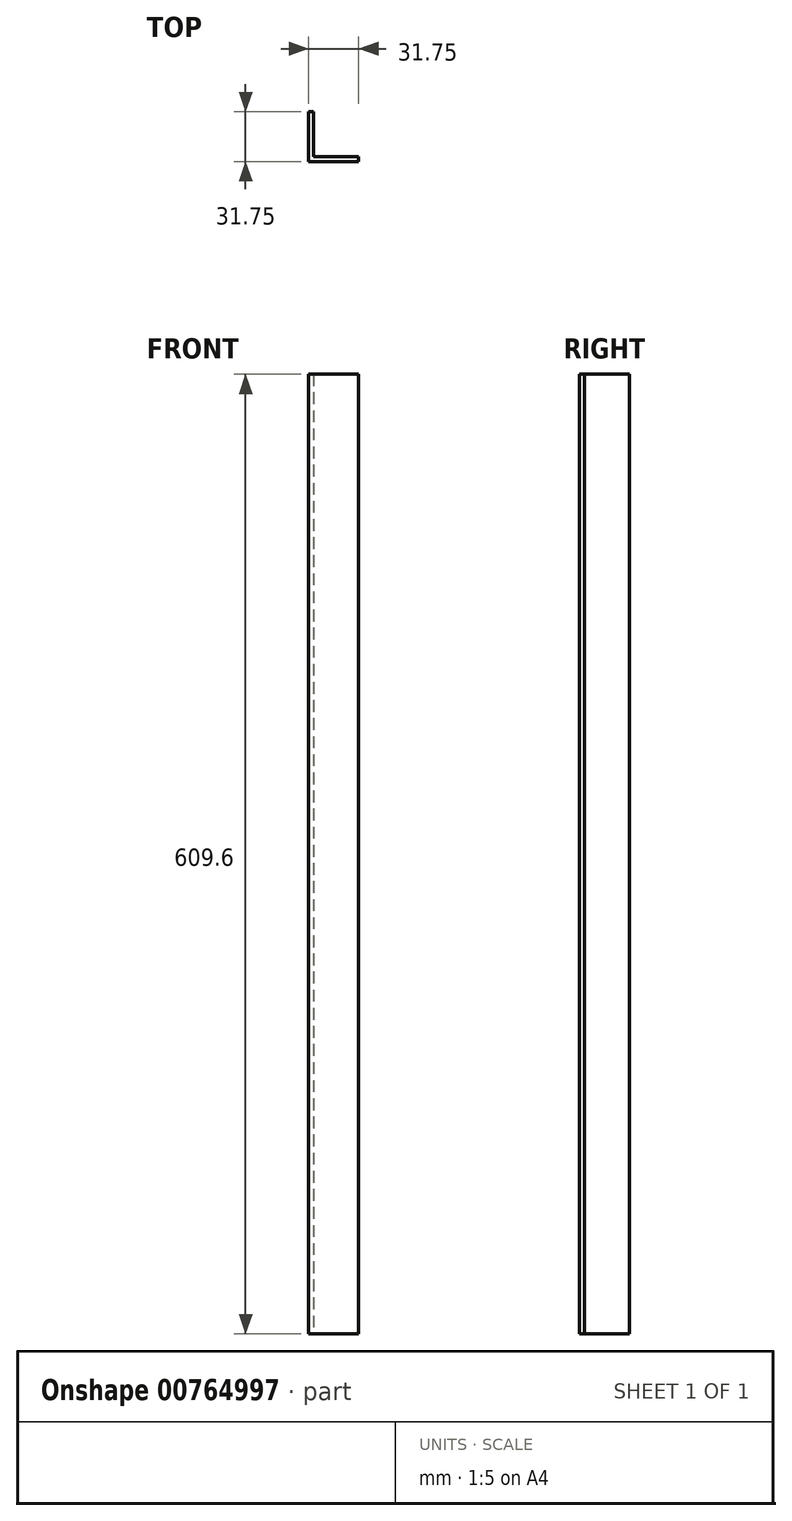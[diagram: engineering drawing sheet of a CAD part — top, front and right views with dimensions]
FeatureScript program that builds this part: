
annotation { "Feature Type Name" : "Feature", "Feature Type Description" : "" }
export const myFeature = defineFeature(function(context is Context, id is Id, definition is map)
    precondition{}
    {
        {
            var Q0;
            Q0=qCreatedBy(makeId("Top.planeOp"),FACE);
            var sketch = newSketch(context, id + "F0", { "sketchPlane" : qUnion([Q0])});
            skLineSegment(sketch, "E0", {"start": v(0, 0) * mm, "end": v(31.75, 0) * mm});
            skLineSegment(sketch, "E1", {"start": v(0, 0) * mm, "end": v(0, 31.75) * mm});
            skLineSegment(sketch, "E2.0", {"start": v(3.05, 3.05) * mm, "end": v(31.75, 3.05) * mm});
            skLineSegment(sketch, "E2.1", {"start": v(3.05, 3.05) * mm, "end": v(3.05, 31.75) * mm});
            skLineSegment(sketch, "E3", {"start": v(0, 31.75) * mm, "end": v(3.05, 31.75) * mm});
            skLineSegment(sketch, "E4", {"start": v(31.75, 3.05) * mm, "end": v(31.75, 0) * mm});
            skSolve(sketch);
        }
        {
            var Q0;
            Q0 = qSketchRegion(id + "F0", true);
            extrude(context, id + "F1", {"entities" : qUnion([Q0]), "depth" : 609.6 * mm, "offsetDistance" : 25.4 * mm});
        }
    });
